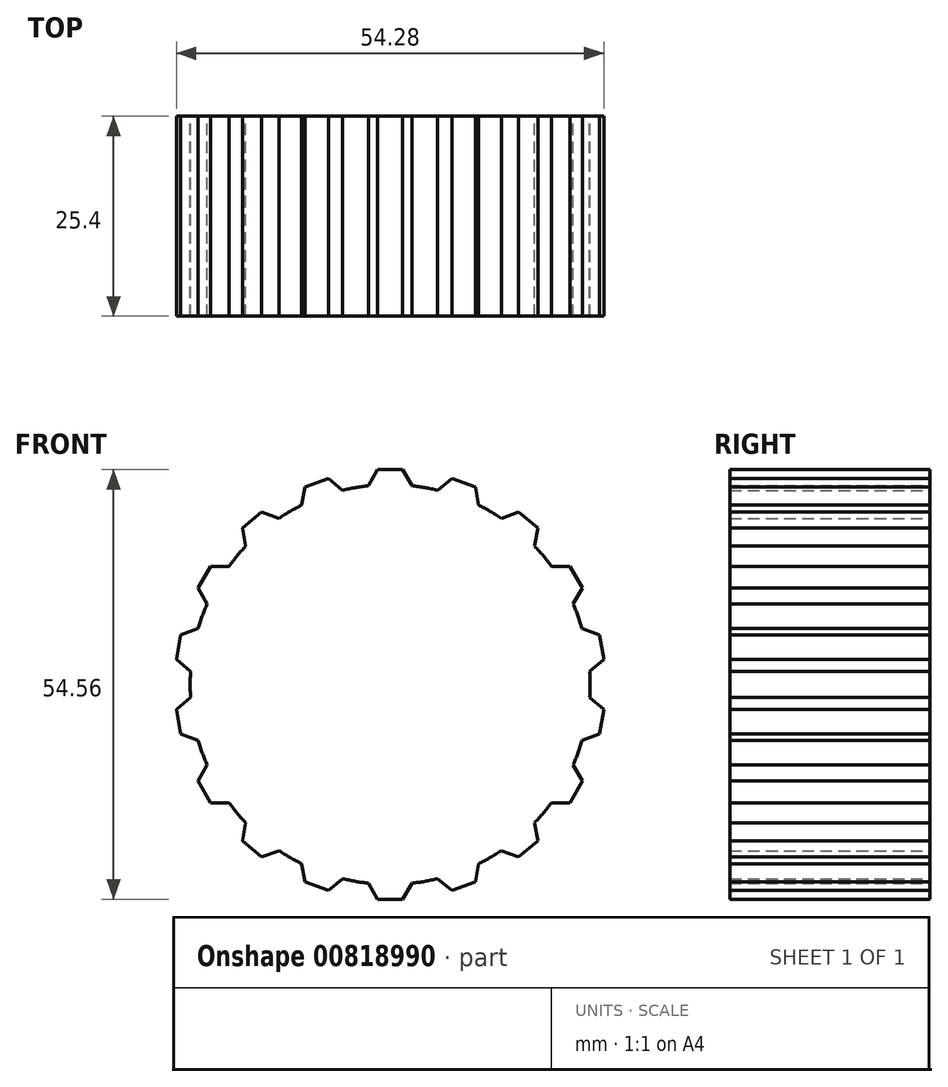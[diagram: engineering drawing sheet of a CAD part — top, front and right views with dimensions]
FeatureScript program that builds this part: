
annotation { "Feature Type Name" : "Feature", "Feature Type Description" : "" }
export const myFeature = defineFeature(function(context is Context, id is Id, definition is map)
    precondition{}
    {
        {
            var Q0;
            Q0=qCreatedBy(makeId("Front.planeOp"),FACE);
            var sketch = newSketch(context, id + "F0", { "sketchPlane" : qUnion([Q0])});
            skArc(sketch, "E0", {"start": v(-2.76, 25.25) * mm, "mid": v(0, -25.4) * mm, "end": v(2.76, 25.25) * mm});
            skLineSegment(sketch, "E1", {"start": v(2.76, 25.25) * mm, "end": v(1.59, 27.28) * mm});
            skLineSegment(sketch, "E2", {"start": v(1.59, 27.28) * mm, "end": v(-1.59, 27.28) * mm});
            skLineSegment(sketch, "E3", {"start": v(-1.59, 27.28) * mm, "end": v(-2.76, 25.25) * mm});
            skLineSegment(sketch, "E4", {"start": v(0, 27.28) * mm, "end": v(0, 0) * mm, "construction": true});
            skLineSegment(sketch, "E5.1.0", {"start": v(-7.84, 26.18) * mm, "end": v(-10.82, 25.1) * mm});
            skLineSegment(sketch, "E5.1.1", {"start": v(-10.82, 25.1) * mm, "end": v(-11.23, 22.78) * mm});
            skLineSegment(sketch, "E5.1.2", {"start": v(-6.04, 24.67) * mm, "end": v(-7.84, 26.18) * mm});
            skLineSegment(sketch, "E5.2.0", {"start": v(-16.32, 21.92) * mm, "end": v(-18.75, 19.88) * mm});
            skLineSegment(sketch, "E5.2.1", {"start": v(-18.75, 19.88) * mm, "end": v(-18.34, 17.57) * mm});
            skLineSegment(sketch, "E5.2.2", {"start": v(-14.12, 21.12) * mm, "end": v(-16.32, 21.92) * mm});
            skLineSegment(sketch, "E5.3.0", {"start": v(-22.83, 15.02) * mm, "end": v(-24.42, 12.27) * mm});
            skLineSegment(sketch, "E5.3.1", {"start": v(-24.42, 12.27) * mm, "end": v(-23.25, 10.23) * mm});
            skLineSegment(sketch, "E5.3.2", {"start": v(-20.49, 15.02) * mm, "end": v(-22.83, 15.02) * mm});
            skLineSegment(sketch, "E5.4.0", {"start": v(-26.6, 6.3) * mm, "end": v(-27.14, 3.17) * mm});
            skLineSegment(sketch, "E5.4.1", {"start": v(-27.14, 3.17) * mm, "end": v(-25.35, 1.67) * mm});
            skLineSegment(sketch, "E5.4.2", {"start": v(-24.39, 7.1) * mm, "end": v(-26.6, 6.3) * mm});
            skLineSegment(sketch, "E5.5.0", {"start": v(-27.14, -3.17) * mm, "end": v(-26.6, -6.3) * mm});
            skLineSegment(sketch, "E5.5.1", {"start": v(-26.6, -6.3) * mm, "end": v(-24.39, -7.1) * mm});
            skLineSegment(sketch, "E5.5.2", {"start": v(-25.35, -1.67) * mm, "end": v(-27.14, -3.17) * mm});
            skLineSegment(sketch, "E5.6.0", {"start": v(-24.42, -12.27) * mm, "end": v(-22.83, -15.02) * mm});
            skLineSegment(sketch, "E5.6.1", {"start": v(-22.83, -15.02) * mm, "end": v(-20.49, -15.02) * mm});
            skLineSegment(sketch, "E5.6.2", {"start": v(-23.25, -10.23) * mm, "end": v(-24.42, -12.27) * mm});
            skLineSegment(sketch, "E5.7.0", {"start": v(-18.75, -19.88) * mm, "end": v(-16.32, -21.92) * mm});
            skLineSegment(sketch, "E5.7.1", {"start": v(-16.32, -21.92) * mm, "end": v(-14.12, -21.12) * mm});
            skLineSegment(sketch, "E5.7.2", {"start": v(-18.34, -17.57) * mm, "end": v(-18.75, -19.88) * mm});
            skLineSegment(sketch, "E5.8.0", {"start": v(-10.82, -25.1) * mm, "end": v(-7.84, -26.18) * mm});
            skLineSegment(sketch, "E5.8.1", {"start": v(-7.84, -26.18) * mm, "end": v(-6.04, -24.67) * mm});
            skLineSegment(sketch, "E5.8.2", {"start": v(-11.23, -22.78) * mm, "end": v(-10.82, -25.1) * mm});
            skLineSegment(sketch, "E5.9.0", {"start": v(-1.59, -27.28) * mm, "end": v(1.59, -27.28) * mm});
            skLineSegment(sketch, "E5.9.1", {"start": v(1.59, -27.28) * mm, "end": v(2.76, -25.25) * mm});
            skLineSegment(sketch, "E5.9.2", {"start": v(-2.76, -25.25) * mm, "end": v(-1.59, -27.28) * mm});
            skLineSegment(sketch, "E5.10.0", {"start": v(7.84, -26.18) * mm, "end": v(10.82, -25.1) * mm});
            skLineSegment(sketch, "E5.10.1", {"start": v(10.82, -25.1) * mm, "end": v(11.23, -22.78) * mm});
            skLineSegment(sketch, "E5.10.2", {"start": v(6.04, -24.67) * mm, "end": v(7.84, -26.18) * mm});
            skLineSegment(sketch, "E5.11.0", {"start": v(16.32, -21.92) * mm, "end": v(18.75, -19.88) * mm});
            skLineSegment(sketch, "E5.11.1", {"start": v(18.75, -19.88) * mm, "end": v(18.34, -17.57) * mm});
            skLineSegment(sketch, "E5.11.2", {"start": v(14.12, -21.12) * mm, "end": v(16.32, -21.92) * mm});
            skLineSegment(sketch, "E5.12.0", {"start": v(22.83, -15.02) * mm, "end": v(24.42, -12.27) * mm});
            skLineSegment(sketch, "E5.12.1", {"start": v(24.42, -12.27) * mm, "end": v(23.25, -10.23) * mm});
            skLineSegment(sketch, "E5.12.2", {"start": v(20.49, -15.02) * mm, "end": v(22.83, -15.02) * mm});
            skLineSegment(sketch, "E5.13.0", {"start": v(26.6, -6.3) * mm, "end": v(27.14, -3.17) * mm});
            skLineSegment(sketch, "E5.13.1", {"start": v(27.14, -3.17) * mm, "end": v(25.35, -1.67) * mm});
            skLineSegment(sketch, "E5.13.2", {"start": v(24.39, -7.1) * mm, "end": v(26.6, -6.3) * mm});
            skLineSegment(sketch, "E5.14.0", {"start": v(27.14, 3.17) * mm, "end": v(26.6, 6.3) * mm});
            skLineSegment(sketch, "E5.14.1", {"start": v(26.6, 6.3) * mm, "end": v(24.39, 7.1) * mm});
            skLineSegment(sketch, "E5.14.2", {"start": v(25.35, 1.67) * mm, "end": v(27.14, 3.17) * mm});
            skLineSegment(sketch, "E5.15.0", {"start": v(24.42, 12.27) * mm, "end": v(22.83, 15.02) * mm});
            skLineSegment(sketch, "E5.15.1", {"start": v(22.83, 15.02) * mm, "end": v(20.49, 15.02) * mm});
            skLineSegment(sketch, "E5.15.2", {"start": v(23.25, 10.23) * mm, "end": v(24.42, 12.27) * mm});
            skLineSegment(sketch, "E5.16.0", {"start": v(18.75, 19.88) * mm, "end": v(16.32, 21.92) * mm});
            skLineSegment(sketch, "E5.16.1", {"start": v(16.32, 21.92) * mm, "end": v(14.12, 21.12) * mm});
            skLineSegment(sketch, "E5.16.2", {"start": v(18.34, 17.57) * mm, "end": v(18.75, 19.88) * mm});
            skLineSegment(sketch, "E5.17.0", {"start": v(10.82, 25.1) * mm, "end": v(7.84, 26.18) * mm});
            skLineSegment(sketch, "E5.17.1", {"start": v(7.84, 26.18) * mm, "end": v(6.04, 24.67) * mm});
            skLineSegment(sketch, "E5.17.2", {"start": v(11.23, 22.78) * mm, "end": v(10.82, 25.1) * mm});
            skSolve(sketch);
        }
        {
            var Q0;
            Q0 = qSketchRegion(id + "F0", true);
            extrude(context, id + "F1", {"entities" : qUnion([Q0]), "depth" : 25.4 * mm, "offsetDistance" : 25.4 * mm});
        }
    });
